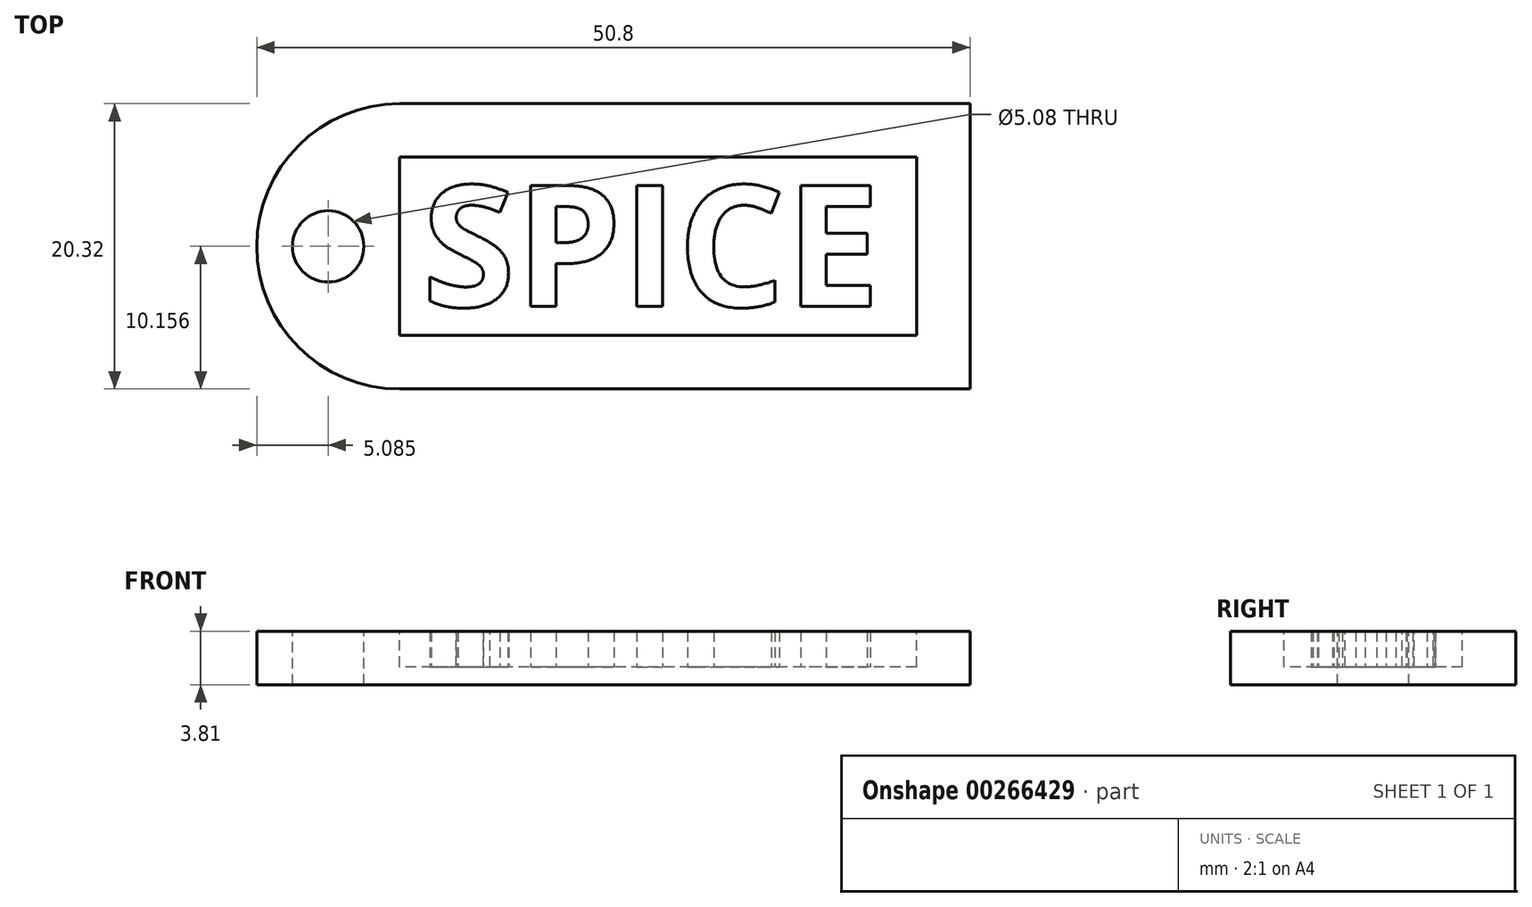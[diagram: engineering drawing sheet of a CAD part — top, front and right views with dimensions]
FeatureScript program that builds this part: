
annotation { "Feature Type Name" : "Feature", "Feature Type Description" : "" }
export const myFeature = defineFeature(function(context is Context, id is Id, definition is map)
    precondition{}
    {
        {
            var Q0;
            Q0=qCreatedBy(makeId("Top.planeOp"),FACE);
            var sketch = newSketch(context, id + "F0", { "sketchPlane" : qUnion([Q0])});
            skLineSegment(sketch, "E0.bottom", {"start": v(-8.27, 25.93) * mm, "end": v(32.37, 25.93) * mm});
            skLineSegment(sketch, "E0.top", {"start": v(-8.27, 5.6) * mm, "end": v(32.37, 5.6) * mm});
            skLineSegment(sketch, "E0.left", {"start": v(-18.43, 15.77) * mm, "end": v(-18.43, 15.77) * mm});
            skLineSegment(sketch, "E0.right", {"start": v(32.37, 25.93) * mm, "end": v(32.37, 5.6) * mm});
            skPoint(sketch, "E1.visualSharp", {"position": v(-18.43, 25.93) * mm});
            skArc(sketch, "E1.filletArc", {"start": v(-8.27, 25.93) * mm, "mid": v(-15.45, 22.95) * mm, "end": v(-18.43, 15.77) * mm});
            skPoint(sketch, "E2.visualSharp", {"position": v(-18.43, 5.6) * mm});
            skArc(sketch, "E2.filletArc", {"start": v(-18.43, 15.77) * mm, "mid": v(-15.45, 8.58) * mm, "end": v(-8.27, 5.6) * mm});
            skSolve(sketch);
        }
        {
            var Q0;
            Q0 = qSketchRegion(id + "F0", true);
            extrude(context, id + "F1", {"entities" : qUnion([Q0]), "depth" : 3.8 * mm});
        }
        {
            var Q0;
            Q0=makeQuery(id+"F1.opExtrude","CAP_FACE",FACE,{"disambiguationData":[OSD([sQuery(id+"F0.wireOp",EDGE,"E0.bottom"),sQuery(id+"F0.wireOp",EDGE,"E0.top"),sQuery(id+"F0.wireOp",EDGE,"E0.right"),sQuery(id+"F0.wireOp",EDGE,"E1.filletArc"),sQuery(id+"F0.wireOp",EDGE,"E2.filletArc")])],"isStart":false});
            var sketch = newSketch(context, id + "F2", { "sketchPlane" : qUnion([Q0])});
            skPoint(sketch, "E3", {"position": v(-8.27, 9.42) * mm});
            skPoint(sketch, "E4", {"position": v(28.56, 22.12) * mm});
            skLineSegment(sketch, "E5.bottom", {"start": v(28.56, 22.12) * mm, "end": v(-8.27, 22.12) * mm});
            skLineSegment(sketch, "E5.top", {"start": v(28.56, 9.42) * mm, "end": v(-8.27, 9.42) * mm});
            skLineSegment(sketch, "E5.left", {"start": v(28.56, 22.12) * mm, "end": v(28.56, 9.42) * mm});
            skLineSegment(sketch, "E5.right", {"start": v(-8.27, 22.12) * mm, "end": v(-8.27, 9.42) * mm});
            skSolve(sketch);
        }
        {
            var Q0;
            Q0 = qSketchRegion(id + "F2", true);
            extrude(context, id + "F3", {"entities" : qUnion([Q0]), "operationType" : NewBodyOperationType.REMOVE, "oppositeDirection" : true, "depth" : 2.54 * mm});
        }
        {
            var Q0;
            Q0=makeQuery(id+"F1.opExtrude","CAP_FACE",FACE,{"disambiguationData":[OSD([sQuery(id+"F0.wireOp",EDGE,"E0.bottom"),sQuery(id+"F0.wireOp",EDGE,"E0.top"),sQuery(id+"F0.wireOp",EDGE,"E0.right"),sQuery(id+"F0.wireOp",EDGE,"E1.filletArc"),sQuery(id+"F0.wireOp",EDGE,"E2.filletArc")])],"isStart":false});
            var sketch = newSketch(context, id + "F4", { "sketchPlane" : qUnion([Q0])});
            skPoint(sketch, "E6", {"position": v(-13.35, 15.77) * mm});
            skPoint(sketch, "E6.positionSnap0", {"position": v(-18.43, 15.77) * mm});
            skCircle(sketch, "E7", {"center": v(-13.35, 15.77) * mm, "radius": 2.54 * mm});
            skSolve(sketch);
        }
        {
            var Q0;
            Q0=makeQuery(id+"F4.imprint","IMPRINT",FACE,{"disambiguationData":[TD([[makeQuery(id+"F4.imprint","IMPRINT",EDGE,{"derivedFrom":sQuery(id+"F4.wireOp",EDGE,"E7")}),1.0]])]});
            extrude(context, id + "F5", {"entities" : qUnion([Q0]), "operationType" : NewBodyOperationType.REMOVE, "oppositeDirection" : true, "depth" : 25.4 * mm});
        }
        {
            var Q0;
            Q0=makeQuery(id+"F3.boolean.opBoolean","COPY",FACE,{"derivedFrom":makeQuery(id+"F3.opExtrude","CAP_FACE",FACE,{"disambiguationData":[OSD([sQuery(id+"F2.wireOp",EDGE,"E5.bottom"),sQuery(id+"F2.wireOp",EDGE,"E5.top"),sQuery(id+"F2.wireOp",EDGE,"E5.left"),sQuery(id+"F2.wireOp",EDGE,"E5.right")])],"isStart":false})});
            var sketch = newSketch(context, id + "F6", { "sketchPlane" : qUnion([Q0])});
            skText(sketch, "E8", { "text": "SPICE", "fontName": "OpenSans-Bold.ttf"});
            const initialGuessF6  = {"E8": [-0.00666, 0.01148, 1, 0, 0.00868]};
            skSetInitialGuess(sketch, initialGuessF6);
            skSolve(sketch);
        }
        {
            var Q0;
            Q0 = qSketchRegion(id + "F6", true);
            extrude(context, id + "F7", {"entities" : qUnion([Q0]), "operationType" : NewBodyOperationType.ADD, "depth" : 2.54 * mm});
        }
    });
